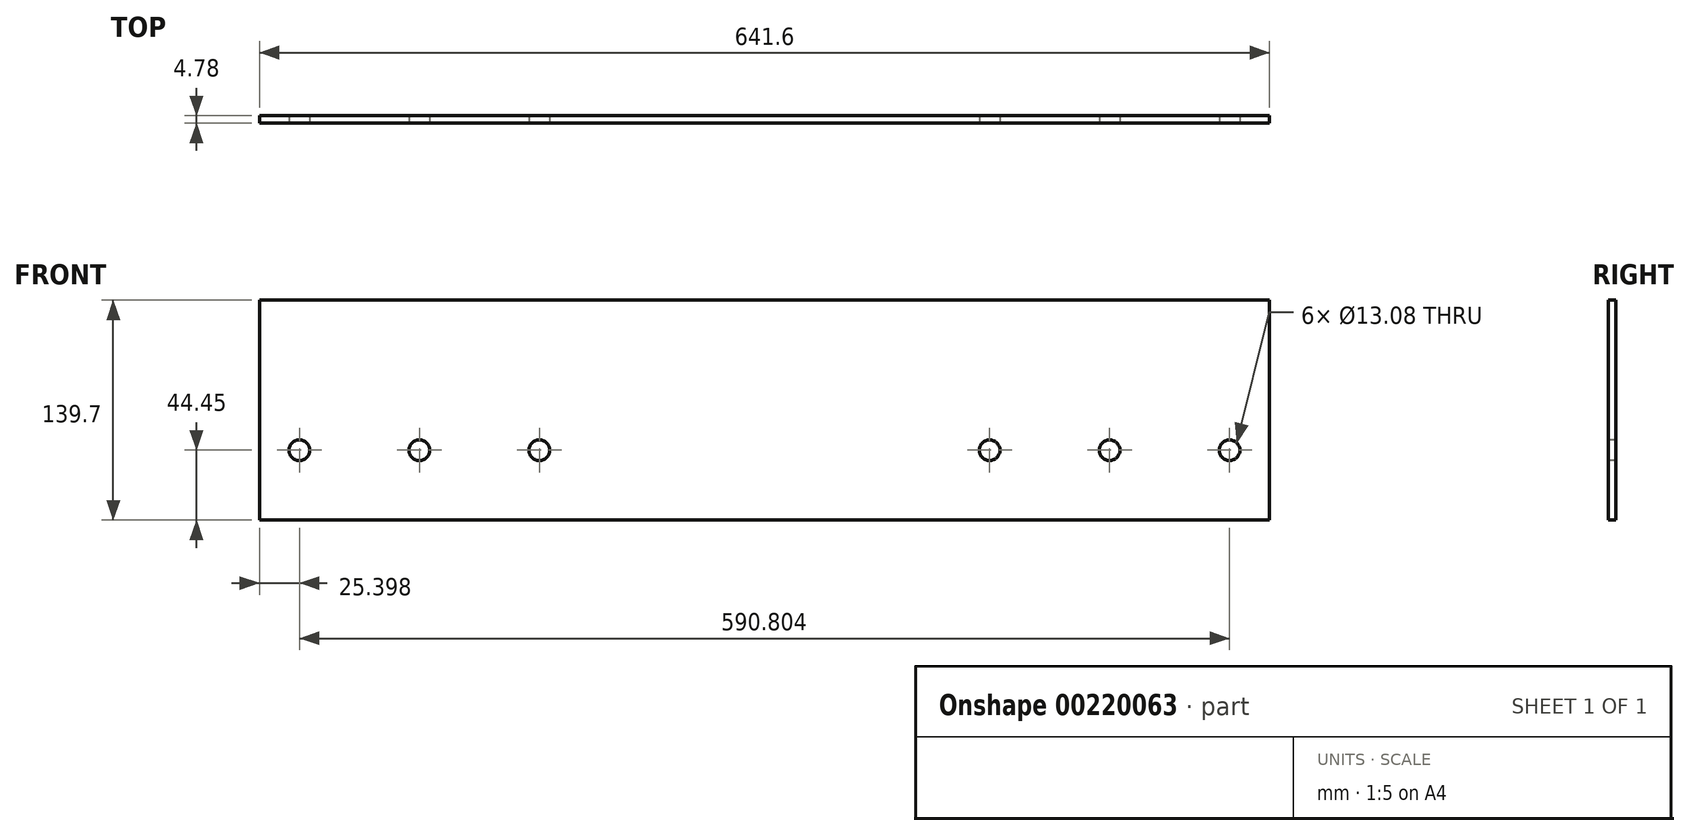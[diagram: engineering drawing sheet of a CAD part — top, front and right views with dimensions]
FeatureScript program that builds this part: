
annotation { "Feature Type Name" : "Feature", "Feature Type Description" : "" }
export const myFeature = defineFeature(function(context is Context, id is Id, definition is map)
    precondition{}
    {
        {
            var Q0;
            Q0=qCreatedBy(makeId("Front.planeOp"),FACE);
            var sketch = newSketch(context, id + "F0", { "sketchPlane" : qUnion([Q0])});
            skLineSegment(sketch, "E0.bottom", {"start": v(320.8, 69.85) * mm, "end": v(-320.8, 69.85) * mm});
            skLineSegment(sketch, "E0.top", {"start": v(320.8, -69.85) * mm, "end": v(-320.8, -69.85) * mm});
            skLineSegment(sketch, "E0.left", {"start": v(320.8, 69.85) * mm, "end": v(320.8, -69.85) * mm});
            skLineSegment(sketch, "E0.right", {"start": v(-320.8, 69.85) * mm, "end": v(-320.8, -69.85) * mm});
            skPoint(sketch, "E0.middle", {"position": v(0, 0) * mm});
            skLineSegment(sketch, "E1", {"start": v(-349.8, -25.4) * mm, "end": v(408.08, -25.4) * mm, "construction": true});
            skCircle(sketch, "E2", {"center": v(295.4, -25.4) * mm, "radius": 6.54 * mm});
            skCircle(sketch, "E3", {"center": v(219.2, -25.4) * mm, "radius": 6.54 * mm});
            skCircle(sketch, "E4", {"center": v(143, -25.4) * mm, "radius": 6.54 * mm});
            skCircle(sketch, "E5", {"center": v(-295.4, -25.4) * mm, "radius": 6.54 * mm});
            skCircle(sketch, "E6", {"center": v(-219.2, -25.4) * mm, "radius": 6.54 * mm});
            skCircle(sketch, "E7", {"center": v(-143, -25.4) * mm, "radius": 6.54 * mm});
            skSolve(sketch);
        }
        {
            var Q0;
            Q0 = qSketchRegion(id + "F0", true);
            extrude(context, id + "F1", {"entities" : qUnion([Q0]), "oppositeDirection" : true, "depth" : 4.78 * mm});
        }
    });
